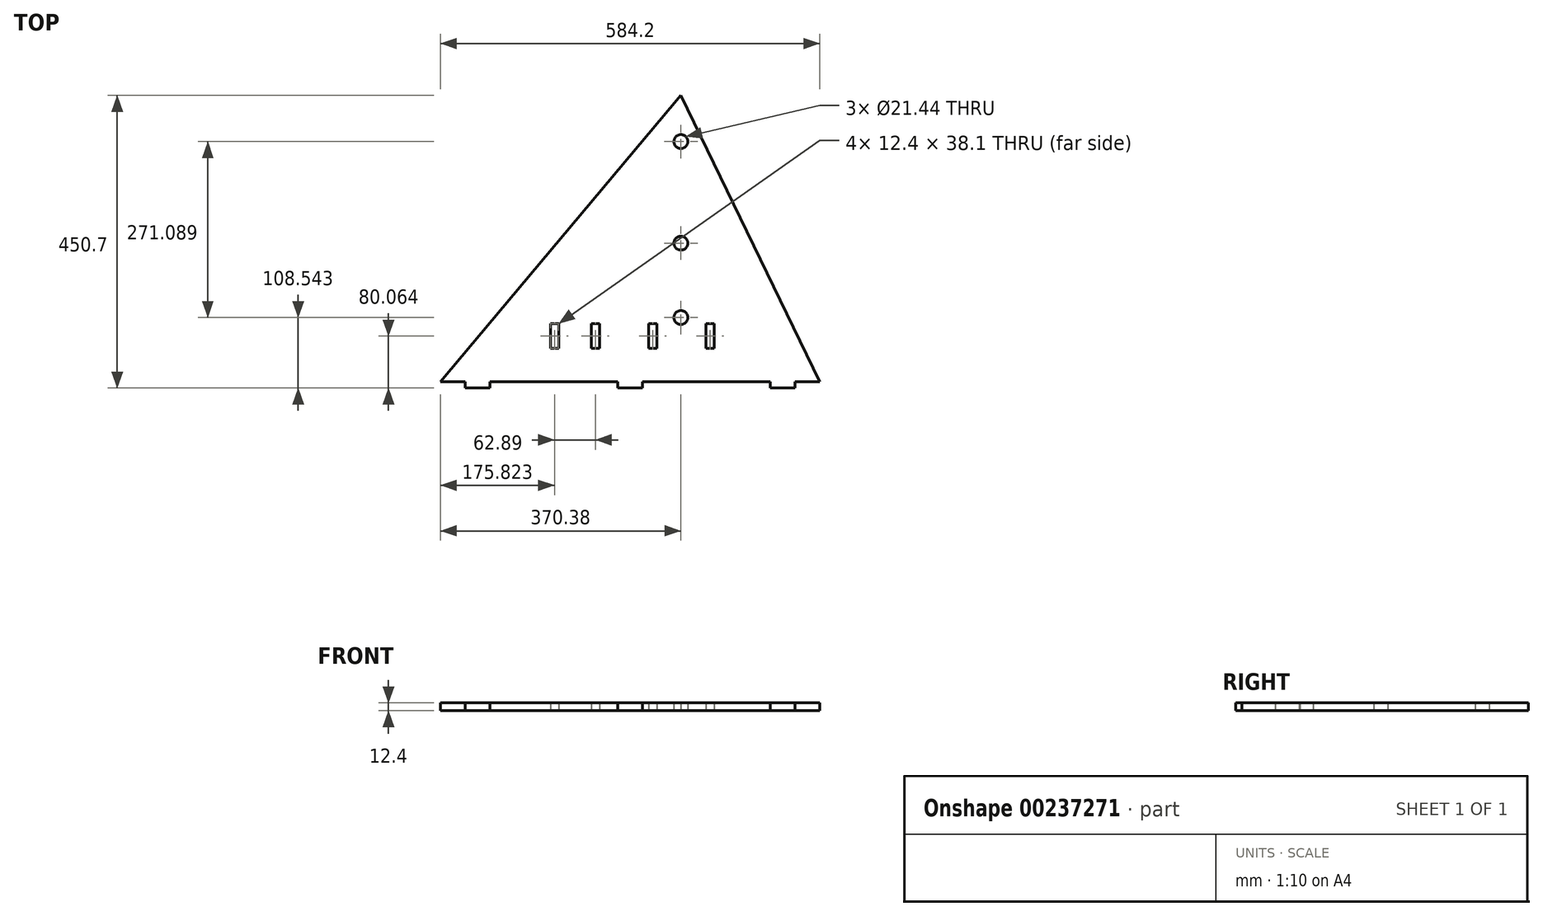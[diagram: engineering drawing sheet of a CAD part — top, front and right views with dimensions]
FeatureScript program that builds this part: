
annotation { "Feature Type Name" : "Feature", "Feature Type Description" : "" }
export const myFeature = defineFeature(function(context is Context, id is Id, definition is map)
    precondition{}
    {
        {
            var Q0;
            Q0=qCreatedBy(makeId("Top.planeOp"),FACE);
            var sketch = newSketch(context, id + "F0", { "sketchPlane" : qUnion([Q0])});
            skLineSegment(sketch, "E0", {"start": v(0, 0) * mm, "end": v(584.2, 0) * mm});
            skLineSegment(sketch, "E1", {"start": v(0, 0) * mm, "end": v(370.38, 441.4) * mm});
            skLineSegment(sketch, "E2", {"start": v(370.38, 441.4) * mm, "end": v(584.2, 0) * mm});
            skLineSegment(sketch, "E3", {"start": v(370.38, 441.4) * mm, "end": v(370.38, 0) * mm, "construction": true});
            skCircle(sketch, "E4", {"center": v(370.38, 99.24) * mm, "radius": 10.72 * mm});
            skCircle(sketch, "E5", {"center": v(370.38, 213.87) * mm, "radius": 10.72 * mm});
            skCircle(sketch, "E6", {"center": v(370.38, 370.33) * mm, "radius": 10.72 * mm});
            skSolve(sketch);
        }
        {
            var Q0;
            Q0=makeQuery(id+"F0.imprint","IMPRINT",FACE,{"disambiguationData":[TD([[makeQuery(id+"F0.imprint","IMPRINT",EDGE,{"derivedFrom":sQuery(id+"F0.wireOp",EDGE,"E0")}),1.0]])]});
            extrude(context, id + "F1", {"entities" : qUnion([Q0]), "depth" : 12.4 * mm});
        }
        {
            var Q0;
            Q0=makeQuery(id+"F1.opExtrude","SWEPT_FACE",FACE,{"disambiguationData":[OSD([sQuery(id+"F0.wireOp",EDGE,"E0")])]});
            var sketch = newSketch(context, id + "F2", { "sketchPlane" : qUnion([Q0])});
            skLineSegment(sketch, "E7.bottom", {"start": v(38.1, 0) * mm, "end": v(76.2, 0) * mm});
            skLineSegment(sketch, "E7.top", {"start": v(38.1, 12.4) * mm, "end": v(76.2, 12.4) * mm});
            skLineSegment(sketch, "E7.left", {"start": v(38.1, 0) * mm, "end": v(38.1, 12.4) * mm});
            skLineSegment(sketch, "E7.right", {"start": v(76.2, 0) * mm, "end": v(76.2, 12.4) * mm});
            skLineSegment(sketch, "E8.bottom", {"start": v(273.05, 0) * mm, "end": v(311.15, 0) * mm});
            skLineSegment(sketch, "E8.top", {"start": v(273.05, 12.4) * mm, "end": v(311.15, 12.4) * mm});
            skLineSegment(sketch, "E8.left", {"start": v(273.05, 0) * mm, "end": v(273.05, 12.4) * mm});
            skLineSegment(sketch, "E8.right", {"start": v(311.15, 0) * mm, "end": v(311.15, 12.4) * mm});
            skLineSegment(sketch, "E9.bottom", {"start": v(546.1, 12.4) * mm, "end": v(508, 12.4) * mm});
            skLineSegment(sketch, "E9.top", {"start": v(546.1, 0) * mm, "end": v(508, 0) * mm});
            skLineSegment(sketch, "E9.left", {"start": v(546.1, 12.4) * mm, "end": v(546.1, 0) * mm});
            skLineSegment(sketch, "E9.right", {"start": v(508, 12.4) * mm, "end": v(508, 0) * mm});
            skSolve(sketch);
        }
        {
            var Q0;
            Q0=makeQuery(id+"F2.imprint","IMPRINT",FACE,{"disambiguationData":[TD([[makeQuery(id+"F2.imprint","IMPRINT",EDGE,{"derivedFrom":sQuery(id+"F2.wireOp",EDGE,"E7.bottom")}),1.0]])]});
            var Q1;
            Q1=makeQuery(id+"F2.imprint","IMPRINT",FACE,{"disambiguationData":[TD([[makeQuery(id+"F2.imprint","IMPRINT",EDGE,{"derivedFrom":sQuery(id+"F2.wireOp",EDGE,"E8.bottom")}),1.0]])]});
            var Q2;
            Q2=makeQuery(id+"F2.imprint","IMPRINT",FACE,{"disambiguationData":[TD([[makeQuery(id+"F2.imprint","IMPRINT",EDGE,{"derivedFrom":sQuery(id+"F2.wireOp",EDGE,"E9.bottom")}),-1.0]])]});
            extrude(context, id + "F3", {"entities" : qUnion([Q0, Q1, Q2]), "operationType" : NewBodyOperationType.ADD, "depth" : 9.3 * mm});
        }
        {
            var Q0;
            Q0=makeQuery(id+"F3.boolean.opBoolean","MERGE",FACE,{"derivedFrom":[makeQuery(id+"F1.opExtrude","CAP_FACE",FACE,{"disambiguationData":[OSD([sQuery(id+"F0.wireOp",EDGE,"E0"),sQuery(id+"F0.wireOp",EDGE,"nA4AqNiE-HoWg-MnKa-9BfH-WNb7xuhupGYB"),sQuery(id+"F0.wireOp",EDGE,"HwJ8IZh8-WwrF-obUk-VoMP-HJlGLo7zmg6s"),sQuery(id+"F0.wireOp",EDGE,"hbV72auo-273c-H3mX-hN14-NdLNeiQO2f8u"),sQuery(id+"F0.wireOp",EDGE,"yJkv0m9N-xar6-jenL-caYz-NCVx4oEyzwZq"),sQuery(id+"F0.wireOp",EDGE,"0IbjTIdv-al9A-gIdp-c788-NeGzfYGJylQS"),sQuery(id+"F0.wireOp",EDGE,"PPQqT81c-MBrL-Zwf6-FBoo-YlBdeRjJLvez"),sQuery(id+"F0.wireOp",EDGE,"1zVKnzYX-4IMU-bpsW-vgjR-UfY4y7IhUxRJ"),sQuery(id+"F0.wireOp",EDGE,"5PhSZh7U-XTF8-9HuU-3B06-5hTz75dbE28A"),sQuery(id+"F0.wireOp",EDGE,"QVwwZdeT-OtHh-xgnp-WqoG-H6M2aq466ZE5"),sQuery(id+"F0.wireOp",EDGE,"ByblHu9g-uYND-DHe2-2H8c-uT3Bsr3WFWiR"),sQuery(id+"F0.wireOp",EDGE,"q02sBKiU-ZI61-Ygqg-VMs2-e9jpUoOFu8LE"),sQuery(id+"F0.wireOp",EDGE,"yCSYR6cb-g6EO-dpne-vkbb-vtuTMJx8oQwn"),sQuery(id+"F0.wireOp",EDGE,"idvjweJo-wAV1-CoL9-3O4M-DzAfA2Q9TY8j"),sQuery(id+"F0.wireOp",EDGE,"c9bJ2uXe-l4rV-DpG6-cNZs-KjiGAo79kyFT"),sQuery(id+"F0.wireOp",EDGE,"7UX84spq-HRxE-01sJ-ZdLk-nk1ZSfVjff84"),sQuery(id+"F0.wireOp",EDGE,"KV4dBIfH-gvWu-Nq0R-Qmzo-mCH37MA8YzNq"),sQuery(id+"F0.wireOp",EDGE,"51JhfH0C-1wzP-8lwW-ZeS3-U5hvUvuMjHKp")])],"isStart":true}),makeQuery(id+"F3.opExtrude","SWEPT_FACE",FACE,{"disambiguationData":[OSD([sQuery(id+"F2.wireOp",EDGE,"E7.bottom")])]}),makeQuery(id+"F3.opExtrude","SWEPT_FACE",FACE,{"disambiguationData":[OSD([sQuery(id+"F2.wireOp",EDGE,"E8.bottom")])]}),makeQuery(id+"F3.opExtrude","SWEPT_FACE",FACE,{"disambiguationData":[OSD([sQuery(id+"F2.wireOp",EDGE,"E9.top")])]})]});
            var sketch = newSketch(context, id + "F4", { "sketchPlane" : qUnion([Q0])});
            skLineSegment(sketch, "E10.bottom", {"start": v(421.5, -89.81) * mm, "end": v(409.1, -89.81) * mm});
            skLineSegment(sketch, "E10.top", {"start": v(421.5, -51.71) * mm, "end": v(409.1, -51.71) * mm});
            skLineSegment(sketch, "E10.left", {"start": v(421.5, -89.81) * mm, "end": v(421.5, -51.71) * mm});
            skLineSegment(sketch, "E10.right", {"start": v(409.1, -89.81) * mm, "end": v(409.1, -51.71) * mm});
            skLineSegment(sketch, "E11.bottom", {"start": v(333.2, -89.81) * mm, "end": v(320.8, -89.81) * mm});
            skLineSegment(sketch, "E11.top", {"start": v(333.2, -51.71) * mm, "end": v(320.8, -51.71) * mm});
            skLineSegment(sketch, "E11.left", {"start": v(333.2, -89.81) * mm, "end": v(333.2, -51.71) * mm});
            skLineSegment(sketch, "E11.right", {"start": v(320.8, -89.81) * mm, "end": v(320.8, -51.71) * mm});
            skLineSegment(sketch, "E12.bottom", {"start": v(244.91, -89.81) * mm, "end": v(232.52, -89.81) * mm});
            skLineSegment(sketch, "E12.top", {"start": v(244.91, -51.71) * mm, "end": v(232.52, -51.71) * mm});
            skLineSegment(sketch, "E12.left", {"start": v(244.91, -89.81) * mm, "end": v(244.91, -51.71) * mm});
            skLineSegment(sketch, "E12.right", {"start": v(232.52, -89.81) * mm, "end": v(232.52, -51.71) * mm});
            skLineSegment(sketch, "E13.bottom", {"start": v(182.02, -89.81) * mm, "end": v(169.63, -89.81) * mm});
            skLineSegment(sketch, "E13.top", {"start": v(182.02, -51.71) * mm, "end": v(169.63, -51.71) * mm});
            skLineSegment(sketch, "E13.left", {"start": v(182.02, -89.81) * mm, "end": v(182.02, -51.71) * mm});
            skLineSegment(sketch, "E13.right", {"start": v(169.63, -89.81) * mm, "end": v(169.63, -51.71) * mm});
            skSolve(sketch);
        }
        {
            var Q0;
            Q0 = qSketchRegion(id + "F4", true);
            extrude(context, id + "F5", {"entities" : qUnion([Q0]), "operationType" : NewBodyOperationType.REMOVE, "endBound" : BoundingType.UP_TO_NEXT, "oppositeDirection" : true, "depth" : 9.3 * mm});
        }
    });
